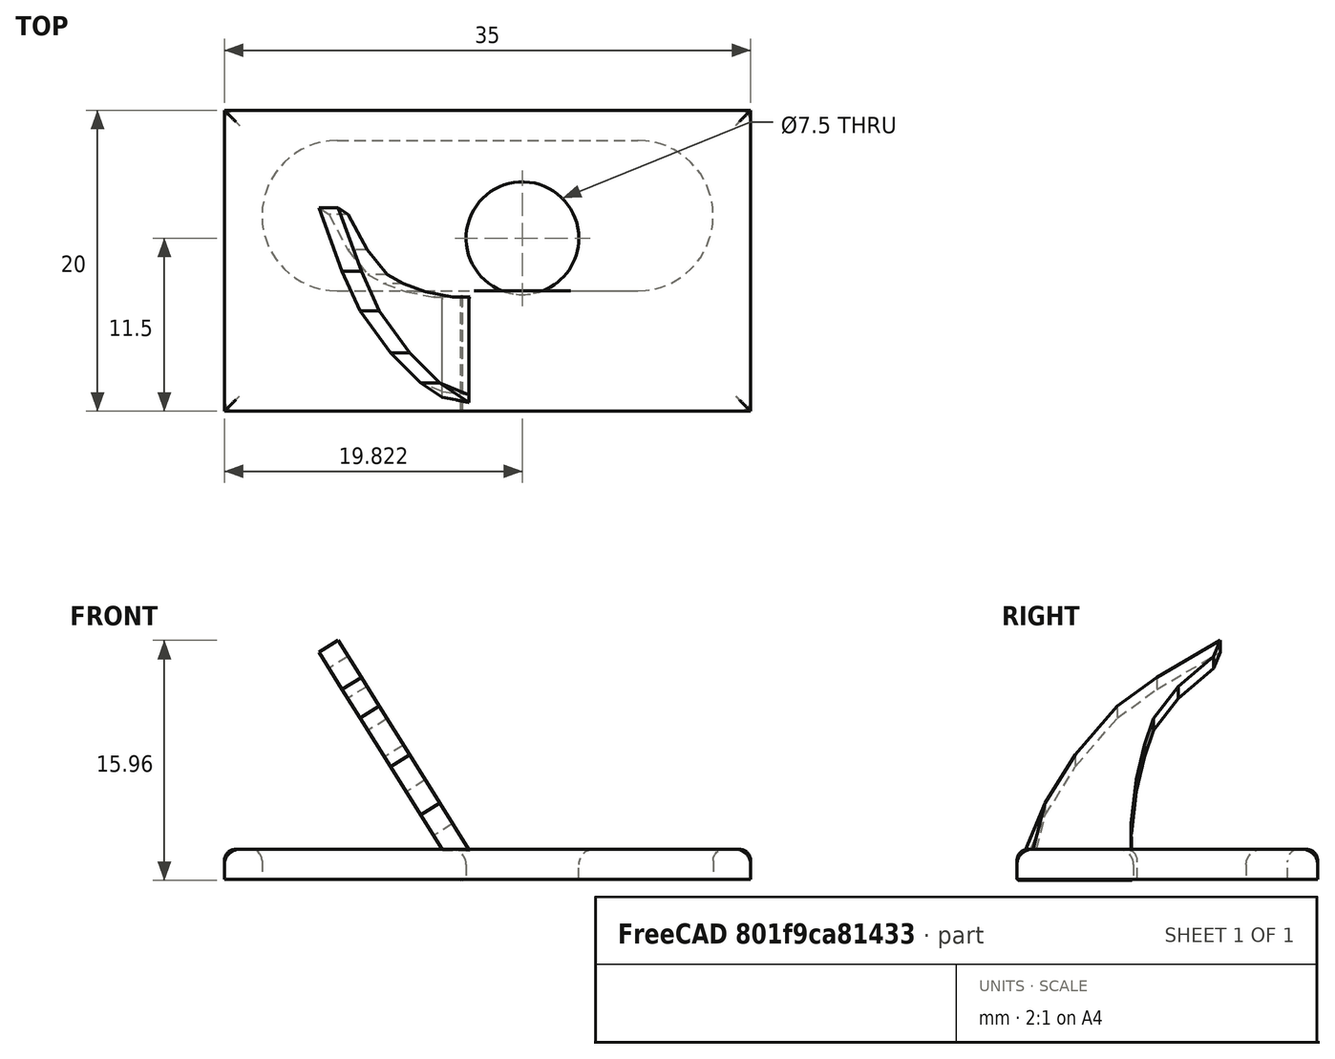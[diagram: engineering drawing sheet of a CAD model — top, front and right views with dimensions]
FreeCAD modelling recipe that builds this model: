
FCSTD DOCUMENT  (FreeCAD 0.20R26155 (Git))
Label: arrow rest
Comment: Print in TPU and use two sided tape to attach over the Bow's plunger
License: Creative Commons Attribution
LicenseURL: http://creativecommons.org/licenses/by/4.0/
objects: Sketcher::SketchObject×4, PartDesign::Pad×4, PartDesign::Plane×2, PartDesign::Fillet×2, PartDesign::Body×2, Mesh::Feature×1
note: 20 computed .brp shape members not serialized (recipe doc carries the construction recipe); baked Part::Feature solids carry a one-line shape summary decoded from their .brp

FEATURE [Sketcher::SketchObject] Sketch
  FullyConstrained = true
  MapMode = 5
  Support = -> [XY_Plane]
  sketch-geometry (8):
    g0: LineSegment StartX=-17.5 StartY=10 StartZ=0 EndX=17.5 EndY=10 EndZ=0
    g1: LineSegment StartX=17.5 StartY=10 StartZ=0 EndX=17.5 EndY=-10 EndZ=0
    g2: LineSegment StartX=17.5 StartY=-10 StartZ=0 EndX=-17.5 EndY=-10 EndZ=0
    g3: LineSegment StartX=-17.5 StartY=-10 StartZ=0 EndX=-17.5 EndY=10 EndZ=0
    g4: ArcOfCircle CenterX=-10 CenterY=3 CenterZ=0 NormalX=0 NormalY=0 NormalZ=1 AngleXU=0 Radius=5 StartAngle=1.5708 EndAngle=4.71239
    g5: ArcOfCircle CenterX=10 CenterY=3 CenterZ=0 NormalX=0 NormalY=0 NormalZ=1 AngleXU=0 Radius=5 StartAngle=4.71239 EndAngle=7.85398
    g6: LineSegment StartX=-10 StartY=-2 StartZ=0 EndX=10 EndY=-2 EndZ=0
    g7: LineSegment StartX=-10 StartY=8 StartZ=0 EndX=10 EndY=8 EndZ=0
  constraints (20):
    c: Coincident(g0,g1)
    c: Coincident(g1,g2)
    c: Coincident(g2,g3)
    c: Coincident(g3,g0)
    c: Horizontal(g0)
    c: Horizontal(g2)
    c: Vertical(g1)
    c: Vertical(g3)
    c: Symmetric(g1,g0,g-1)
    c: DistanceY(g1,g1) = 20
    c: DistanceX(g0,g0) = 35
    c: Tangent(g4,g7) = 1.5708
    c: Tangent(g4,g6) = -1.5708
    c: Tangent(g6,g5) = -1.5708
    c: Tangent(g7,g5) = 1.5708
    c: Equal(g4,g5)
    c: DistanceY(g5,g5) = 10
    c: DistanceX(g7,g7) = 20
    c: Symmetric(g4,g5,g-2)
    c: DistanceY(g5,g0) = 2
FEATURE [PartDesign::Pad] Pad
  Direction = (1,1,1)
  Length = 2
  Length2 = 100
  Profile = -> Sketch
  Type = 0
FEATURE [PartDesign::Plane] DatumPlane
  AttachmentOffset = pos=(0,0,0) rot=(1,0,0;-0.558505rad)
  Length = 61.7387
  MapMode = 5
  Placement = pos=(0,0,0) rot=(-0.436245,-0.436245,-0.787007;4.47513rad)
  ResizeMode = 0
  Support = -> [YZ_Plane]
  Width = 80.6371
FEATURE [PartDesign::Fillet] Fillet
  Base = -> Pad [Face10,Edge5,Edge2,Edge1,Edge8]
  BaseFeature = -> Pad
  Radius = 0.75
  SupportTransform = false
FEATURE [Sketcher::SketchObject] Sketch001
  FullyConstrained = false
  MapMode = 5
  Placement = pos=(0,0,0) rot=(0.436245,0.436245,0.787007;1.80806rad)
  Support = -> [DatumPlane]
  sketch-geometry (13):
    g0: LineSegment StartX=-9.95377 StartY=0.867637 StartZ=0 EndX=-8.1143 EndY=5.98256 EndZ=0
    g1: LineSegment StartX=-8.1143 StartY=5.98256 StartZ=0 EndX=-6.11951 EndY=9.78235 EndZ=0
    g2: LineSegment StartX=-6.11951 StartY=9.78235 StartZ=0 EndX=-3.32039 EndY=13.5993 EndZ=0
    g3: LineSegment StartX=-3.32039 StartY=13.5993 StartZ=0 EndX=-0.709528 EndY=15.852 EndZ=0
    g4: LineSegment StartX=0.719153 StartY=15.1315 StartZ=0 EndX=-0.917319 EndY=12.611 EndZ=0
    g5: LineSegment StartX=-0.917319 StartY=12.611 StartZ=0 EndX=-1.53185 EndY=10.5401 EndZ=0
    g6: LineSegment StartX=-1.53185 StartY=10.5401 StartZ=0 EndX=-2.0635 EndY=7.81216 EndZ=0
    g7: LineSegment StartX=-2.0635 StartY=7.81216 StartZ=0 EndX=-2.39651 EndY=4.36899 EndZ=0
    g8: LineSegment StartX=-2.39651 StartY=4.36899 StartZ=0 EndX=-2.34738 EndY=0.867637 EndZ=0
    g9: LineSegment StartX=-2.34738 StartY=0.867637 StartZ=0 EndX=-9.95377 EndY=0.867637 EndZ=0
    g10: LineSegment StartX=-0.709528 StartY=15.852 StartZ=0 EndX=3.5265 EndY=18.7447 EndZ=0
    g11: LineSegment StartX=3.5265 StartY=18.7447 StartZ=0 EndX=3.07432 EndY=17.5019 EndZ=0
    g12: LineSegment StartX=3.07432 StartY=17.5019 StartZ=0 EndX=0.719153 EndY=15.1315 EndZ=0
  constraints (14):
    c: Coincident(g0,g1)
    c: Coincident(g5,g6)
    c: Coincident(g6,g7)
    c: Coincident(g7,g8)
    c: Coincident(g8,g9)
    c: Coincident(g9,g0)
    c: Horizontal(g9)
    c: Coincident(g1,g2)
    c: Coincident(g3,g2)
    c: Coincident(g5,g4)
    c: Coincident(g3,g10)
    c: Coincident(g10,g11)
    c: Coincident(g11,g12)
    c: Coincident(g12,g4)
FEATURE [PartDesign::Pad] Pad001
  BaseFeature = -> Fillet
  Direction = (1,1,1)
  Length = 1.5
  Length2 = 100
  Profile = -> Sketch001
  Reversed = true
  Type = 0
FEATURE [PartDesign::Body] Body  label="slot rest"
  Group = -> [Sketch,Pad,DatumPlane,Fillet,Sketch001,Pad001]
  Origin = -> Origin
  Tip = -> Pad001
FEATURE [PartDesign::Plane] DatumPlane001
  AttachmentOffset = pos=(0,0,0) rot=(1,0,0;-0.558505rad)
  Length = 61.7387
  MapMode = 5
  Placement = pos=(0,0,0) rot=(-0.436245,-0.436245,-0.787007;4.47513rad)
  ResizeMode = 0
  Support = -> [YZ_Plane001]
  Width = 80.6371
FEATURE [Sketcher::SketchObject] Sketch002
  FullyConstrained = false
  MapMode = 5
  Support = -> [XY_Plane001]
  sketch-geometry (5):
    g0: LineSegment StartX=-17.5 StartY=10 StartZ=0 EndX=17.5 EndY=10 EndZ=0
    g1: LineSegment StartX=17.5 StartY=10 StartZ=0 EndX=17.5 EndY=-10 EndZ=0
    g2: LineSegment StartX=17.5 StartY=-10 StartZ=0 EndX=-17.5 EndY=-10 EndZ=0
    g3: LineSegment StartX=-17.5 StartY=-10 StartZ=0 EndX=-17.5 EndY=10 EndZ=0
    g4: Circle CenterX=2.3224 CenterY=1.5 CenterZ=0 NormalX=0 NormalY=0 NormalZ=1 AngleXU=0 Radius=3.75
  constraints (13):
    c: Coincident(g0,g1)
    c: Coincident(g1,g2)
    c: Coincident(g2,g3)
    c: Coincident(g3,g0)
    c: Horizontal(g0)
    c: Horizontal(g2)
    c: Vertical(g1)
    c: Vertical(g3)
    c: Symmetric(g1,g0,g-1)
    c: DistanceY(g1,g1) = 20
    c: DistanceX(g0,g0) = 35
    c: Diameter(g4) = 7.5
    c: DistanceY(g-1,g4) = 1.5
FEATURE [PartDesign::Pad] Pad002
  Direction = (1,1,1)
  Length = 2
  Length2 = 100
  Profile = -> Sketch002
  Type = 0
FEATURE [Sketcher::SketchObject] Sketch003
  FullyConstrained = false
  MapMode = 5
  Placement = pos=(0,0,0) rot=(0.436245,0.436245,0.787007;1.80806rad)
  Support = -> [DatumPlane001]
  sketch-geometry (13):
    g0: LineSegment StartX=-9.16693 StartY=1.20975 StartZ=0 EndX=-8.1143 EndY=5.98256 EndZ=0
    g1: LineSegment StartX=-8.1143 StartY=5.98256 StartZ=0 EndX=-6.11951 EndY=9.78235 EndZ=0
    g2: LineSegment StartX=-6.11951 StartY=9.78235 StartZ=0 EndX=-3.32039 EndY=13.5993 EndZ=0
    g3: LineSegment StartX=-3.32039 StartY=13.5993 StartZ=0 EndX=-0.709528 EndY=15.852 EndZ=0
    g4: LineSegment StartX=0.719153 StartY=15.1315 StartZ=0 EndX=-0.917319 EndY=12.611 EndZ=0
    g5: LineSegment StartX=-0.917319 StartY=12.611 StartZ=0 EndX=-1.53185 EndY=10.5401 EndZ=0
    g6: LineSegment StartX=-1.53185 StartY=10.5401 StartZ=0 EndX=-2.0635 EndY=7.81216 EndZ=0
    g7: LineSegment StartX=-2.0635 StartY=7.81216 StartZ=0 EndX=-2.39651 EndY=4.36899 EndZ=0
    g8: LineSegment StartX=-2.39651 StartY=4.36899 StartZ=0 EndX=-2.44401 EndY=1.20975 EndZ=0
    g9: LineSegment StartX=-2.44401 StartY=1.20975 StartZ=0 EndX=-9.16693 EndY=1.20975 EndZ=0
    g10: LineSegment StartX=-0.709528 StartY=15.852 StartZ=0 EndX=3.5265 EndY=18.7447 EndZ=0
    g11: LineSegment StartX=3.5265 StartY=18.7447 StartZ=0 EndX=3.07432 EndY=17.5019 EndZ=0
    g12: LineSegment StartX=3.07432 StartY=17.5019 StartZ=0 EndX=0.719153 EndY=15.1315 EndZ=0
  constraints (14):
    c: Coincident(g0,g1)
    c: Coincident(g5,g6)
    c: Coincident(g6,g7)
    c: Coincident(g7,g8)
    c: Coincident(g8,g9)
    c: Coincident(g9,g0)
    c: Horizontal(g9)
    c: Coincident(g1,g2)
    c: Coincident(g3,g2)
    c: Coincident(g5,g4)
    c: Coincident(g3,g10)
    c: Coincident(g10,g11)
    c: Coincident(g11,g12)
    c: Coincident(g12,g4)
FEATURE [PartDesign::Fillet] Fillet001
  Base = -> Pad002 [Face7]
  BaseFeature = -> Pad002
  Radius = 1
  SupportTransform = false
FEATURE [PartDesign::Pad] Pad003  label="Arrow Rest"
  BaseFeature = -> Fillet001
  Direction = (1,1,1)
  Length = 1.5
  Length2 = 100
  Profile = -> Sketch003
  Reversed = true
  Type = 0
FEATURE [PartDesign::Body] Body001  label="hole rest"
  Group = -> [Sketch002,Pad002,Fillet001,DatumPlane001,Sketch003,Pad003]
  Origin = -> Origin001
  Tip = -> Pad003
FEATURE [Mesh::Feature] Mesh  label="Arrow Rest (Meshed)"
